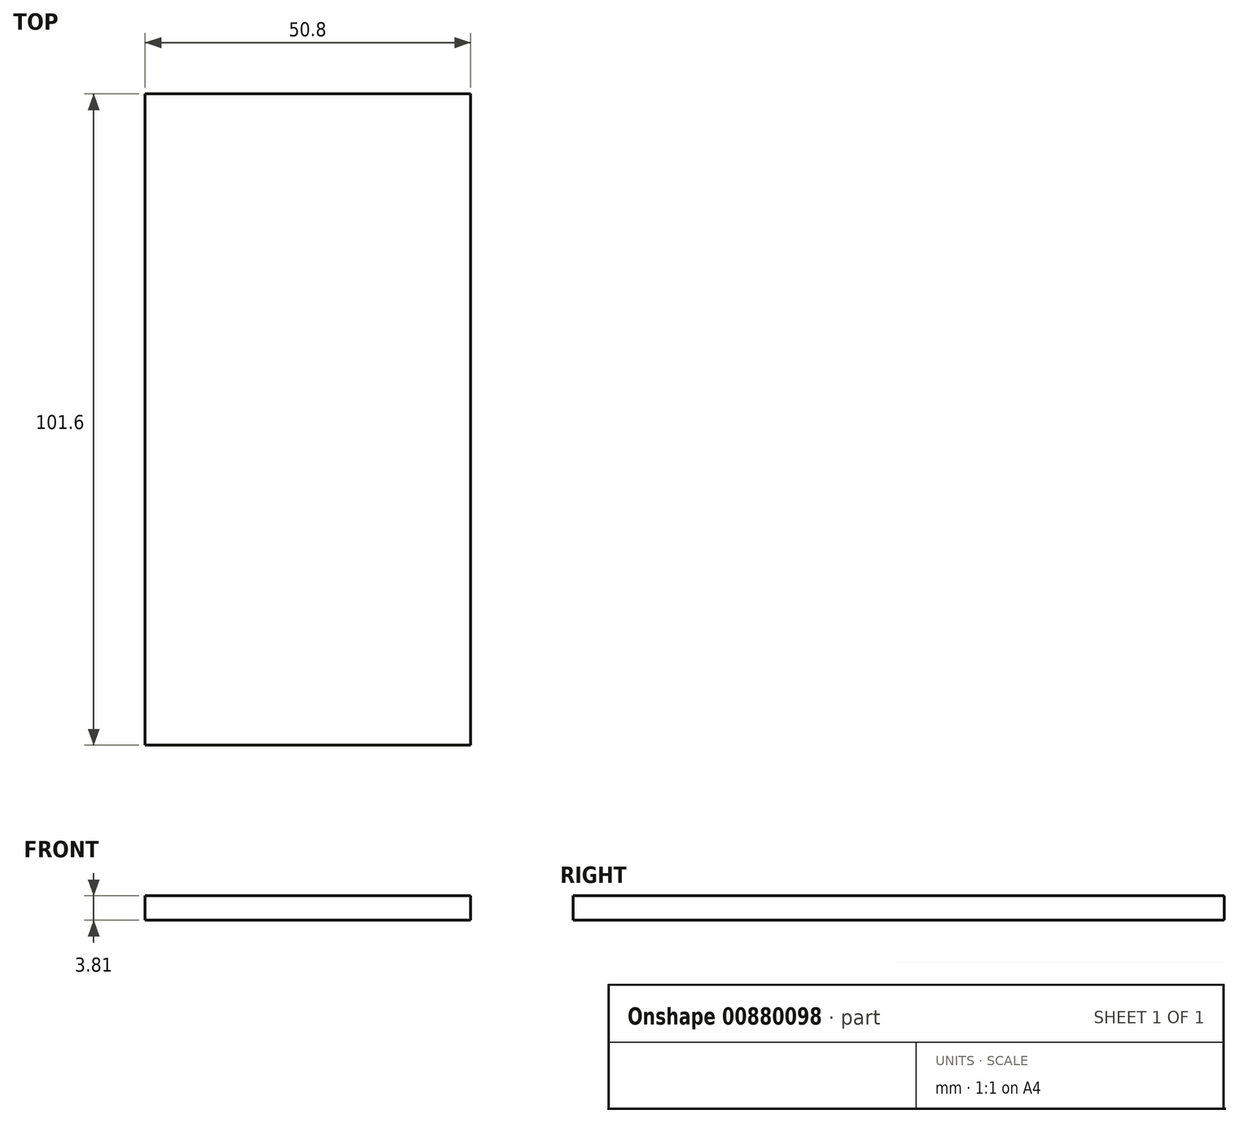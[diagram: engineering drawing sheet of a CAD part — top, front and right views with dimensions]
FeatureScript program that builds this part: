
annotation { "Feature Type Name" : "Feature", "Feature Type Description" : "" }
export const myFeature = defineFeature(function(context is Context, id is Id, definition is map)
    precondition{}
    {
        {
            var Q0;
            Q0=qCreatedBy(makeId("Top.planeOp"),FACE);
            var sketch = newSketch(context, id + "F0", { "sketchPlane" : qUnion([Q0])});
            skLineSegment(sketch, "E0.bottom", {"start": v(0, 0) * mm, "end": v(50.8, 0) * mm});
            skLineSegment(sketch, "E0.top", {"start": v(0, 101.6) * mm, "end": v(50.8, 101.6) * mm});
            skLineSegment(sketch, "E0.left", {"start": v(0, 0) * mm, "end": v(0, 101.6) * mm});
            skLineSegment(sketch, "E0.right", {"start": v(50.8, 0) * mm, "end": v(50.8, 101.6) * mm});
            skSolve(sketch);
        }
        {
            var Q0;
            Q0 = qSketchRegion(id + "F0", true);
            extrude(context, id + "F1", {"entities" : qUnion([Q0]), "depth" : 3.8 * mm, "offsetDistance" : 25.4 * mm});
        }
    });
